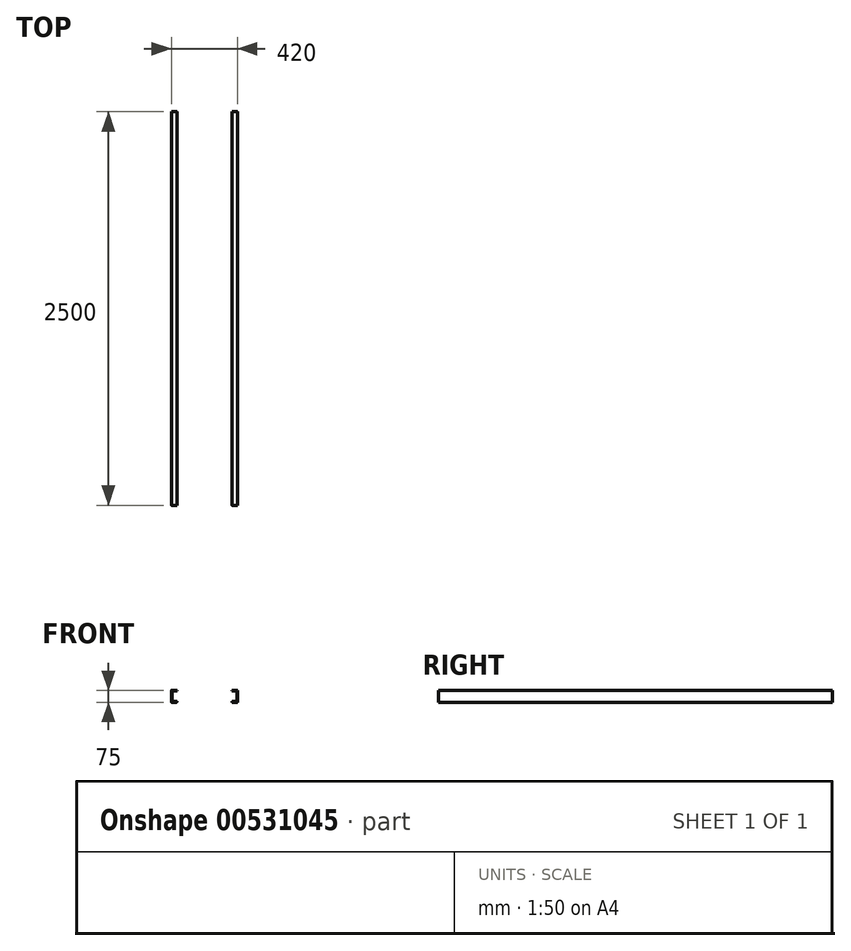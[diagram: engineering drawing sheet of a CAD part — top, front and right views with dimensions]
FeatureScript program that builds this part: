
annotation { "Feature Type Name" : "Feature", "Feature Type Description" : "" }
export const myFeature = defineFeature(function(context is Context, id is Id, definition is map)
    precondition{}
    {
        {
            var Q0;
            Q0=qCreatedBy(makeId("Front.planeOp"),FACE);
            var sketch = newSketch(context, id + "F0", { "sketchPlane" : qUnion([Q0])});
            skLineSegment(sketch, "E0", {"start": v(-205, 33.5) * mm, "end": v(-176, 33.5) * mm});
            skLineSegment(sketch, "E1", {"start": v(-175, 34.5) * mm, "end": v(-175, 36.5) * mm});
            skLineSegment(sketch, "E2", {"start": v(-176, 37.5) * mm, "end": v(-209, 37.5) * mm});
            skLineSegment(sketch, "E3", {"start": v(-210, 36.5) * mm, "end": v(-210, -36.5) * mm});
            skLineSegment(sketch, "E4", {"start": v(-209, -37.5) * mm, "end": v(-176, -37.5) * mm});
            skLineSegment(sketch, "E5", {"start": v(-175, -36.5) * mm, "end": v(-175, -34.5) * mm});
            skLineSegment(sketch, "E6", {"start": v(-176, -33.5) * mm, "end": v(-205, -33.5) * mm});
            skLineSegment(sketch, "E7", {"start": v(-206, -32.5) * mm, "end": v(-206, 32.5) * mm});
            skPoint(sketch, "E8", {"position": v(-210, 0) * mm});
            skPoint(sketch, "E9.visualSharp", {"position": v(-175, 37.5) * mm});
            skArc(sketch, "E9.filletArc", {"start": v(-175, 36.5) * mm, "mid": v(-175.3, 37.2) * mm, "end": v(-176, 37.5) * mm});
            skPoint(sketch, "E10.visualSharp", {"position": v(-175, 33.5) * mm});
            skArc(sketch, "E10.filletArc", {"start": v(-176, 33.5) * mm, "mid": v(-175.3, 33.8) * mm, "end": v(-175, 34.5) * mm});
            skPoint(sketch, "E11.visualSharp", {"position": v(-175, -33.5) * mm});
            skArc(sketch, "E11.filletArc", {"start": v(-175, -34.5) * mm, "mid": v(-175.3, -33.8) * mm, "end": v(-176, -33.5) * mm});
            skPoint(sketch, "E12.visualSharp", {"position": v(-175, -37.5) * mm});
            skArc(sketch, "E12.filletArc", {"start": v(-176, -37.5) * mm, "mid": v(-175.3, -37.2) * mm, "end": v(-175, -36.5) * mm});
            skPoint(sketch, "E13.visualSharp", {"position": v(-206, -33.5) * mm});
            skArc(sketch, "E13.filletArc", {"start": v(-206, -32.5) * mm, "mid": v(-205.7, -33.2) * mm, "end": v(-205, -33.5) * mm});
            skPoint(sketch, "E14.visualSharp", {"position": v(-210, -37.5) * mm});
            skArc(sketch, "E14.filletArc", {"start": v(-210, -36.5) * mm, "mid": v(-209.7, -37.2) * mm, "end": v(-209, -37.5) * mm});
            skPoint(sketch, "E15.visualSharp", {"position": v(-206, 33.5) * mm});
            skArc(sketch, "E15.filletArc", {"start": v(-205, 33.5) * mm, "mid": v(-205.7, 33.2) * mm, "end": v(-206, 32.5) * mm});
            skPoint(sketch, "E16.visualSharp", {"position": v(-210, 37.5) * mm});
            skArc(sketch, "E16.filletArc", {"start": v(-209, 37.5) * mm, "mid": v(-209.7, 37.2) * mm, "end": v(-210, 36.5) * mm});
            skArc(sketch, "E17.MirrorCS", {"start": v(206, -32.5) * mm, "mid": v(205.7, -33.2) * mm, "end": v(205, -33.5) * mm});
            skArc(sketch, "E18.MirrorCS", {"start": v(176, -37.5) * mm, "mid": v(175.3, -37.2) * mm, "end": v(175, -36.5) * mm});
            skArc(sketch, "E19.MirrorCS", {"start": v(175, -34.5) * mm, "mid": v(175.3, -33.8) * mm, "end": v(176, -33.5) * mm});
            skArc(sketch, "E20.MirrorCS", {"start": v(209, 37.5) * mm, "mid": v(209.7, 37.2) * mm, "end": v(210, 36.5) * mm});
            skArc(sketch, "E21.MirrorCS", {"start": v(205, 33.5) * mm, "mid": v(205.7, 33.2) * mm, "end": v(206, 32.5) * mm});
            skArc(sketch, "E22.MirrorCS", {"start": v(176, 33.5) * mm, "mid": v(175.3, 33.8) * mm, "end": v(175, 34.5) * mm});
            skArc(sketch, "E23.MirrorCS", {"start": v(175, 36.5) * mm, "mid": v(175.3, 37.2) * mm, "end": v(176, 37.5) * mm});
            skLineSegment(sketch, "E24.MirrorCS", {"start": v(175, 34.5) * mm, "end": v(175, 36.5) * mm});
            skArc(sketch, "E25.MirrorCS", {"start": v(210, -36.5) * mm, "mid": v(209.7, -37.2) * mm, "end": v(209, -37.5) * mm});
            skLineSegment(sketch, "E26.MirrorCS", {"start": v(175, -36.5) * mm, "end": v(175, -34.5) * mm});
            skPoint(sketch, "E27.MirrorP", {"position": v(175, -37.5) * mm});
            skPoint(sketch, "E28.MirrorP", {"position": v(206, -33.5) * mm});
            skPoint(sketch, "E29.MirrorP", {"position": v(175, -33.5) * mm});
            skPoint(sketch, "E30.MirrorP", {"position": v(175, 33.5) * mm});
            skPoint(sketch, "E31.MirrorP", {"position": v(210, -37.5) * mm});
            skPoint(sketch, "E32.MirrorP", {"position": v(175, 37.5) * mm});
            skPoint(sketch, "E33.MirrorP", {"position": v(210, 37.5) * mm});
            skLineSegment(sketch, "E34.MirrorCS", {"start": v(205, 33.5) * mm, "end": v(176, 33.5) * mm});
            skLineSegment(sketch, "E35.MirrorCS", {"start": v(206, -32.5) * mm, "end": v(206, 32.5) * mm});
            skPoint(sketch, "E36.MirrorP", {"position": v(210, 0) * mm});
            skLineSegment(sketch, "E37.MirrorCS", {"start": v(176, -33.5) * mm, "end": v(205, -33.5) * mm});
            skLineSegment(sketch, "E38.MirrorCS", {"start": v(210, 36.5) * mm, "end": v(210, -36.5) * mm});
            skLineSegment(sketch, "E39.MirrorCS", {"start": v(209, -37.5) * mm, "end": v(176, -37.5) * mm});
            skLineSegment(sketch, "E40.MirrorCS", {"start": v(176, 37.5) * mm, "end": v(209, 37.5) * mm});
            skPoint(sketch, "E41.MirrorP", {"position": v(206, 33.5) * mm});
            skSolve(sketch);
        }
        {
            var Q0;
            Q0 = qSketchRegion(id + "F0", true);
            extrude(context, id + "F1", {"entities" : qUnion([Q0]), "depth" : 2500 * mm, "offsetDistance" : 25 * mm});
        }
    });
